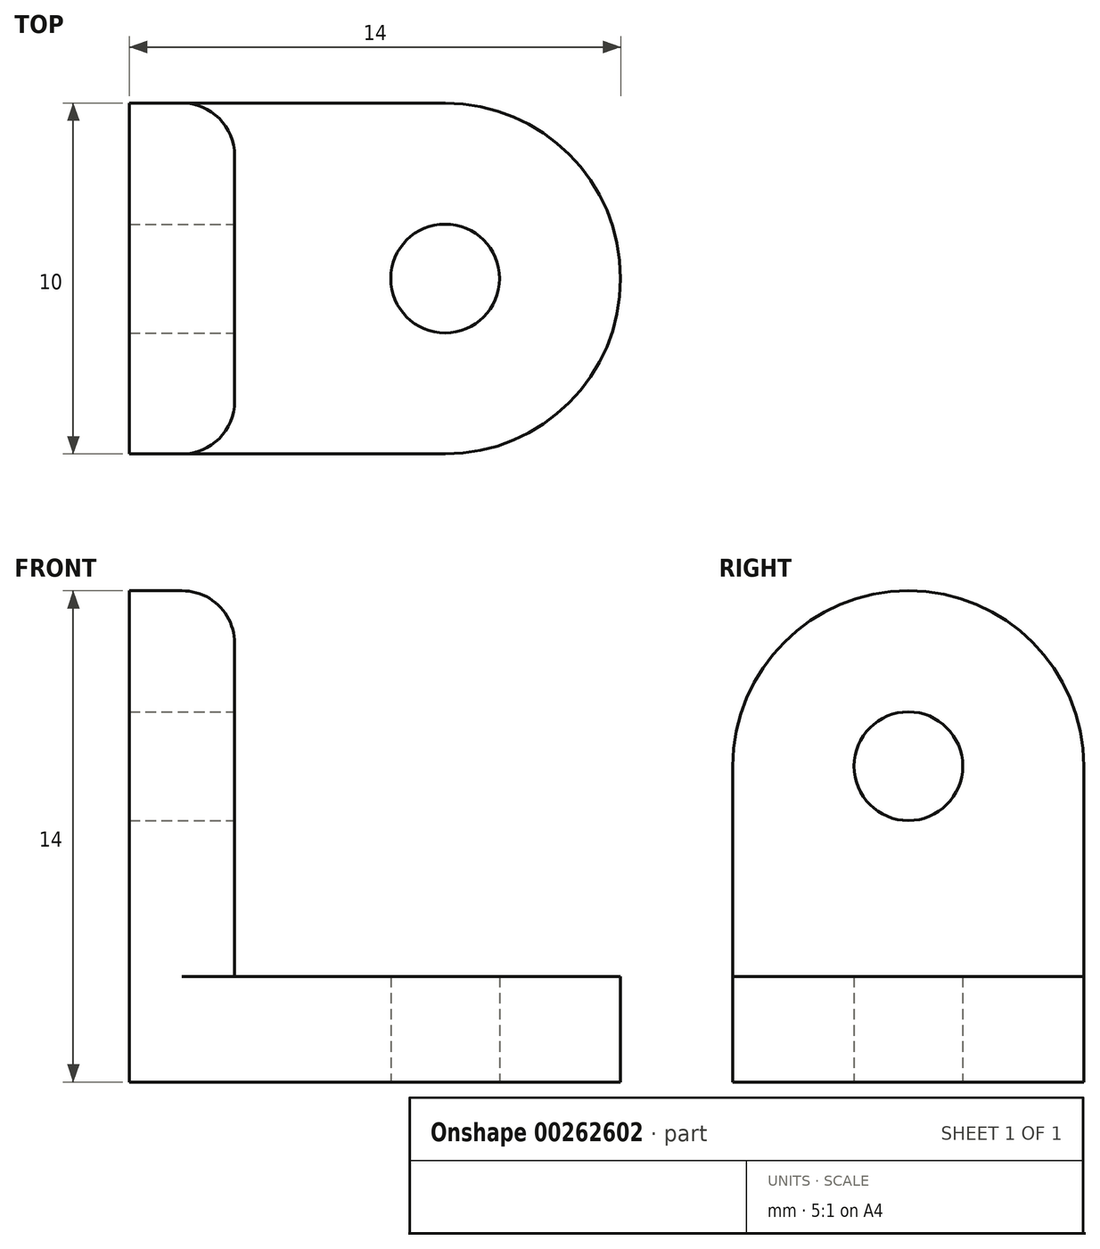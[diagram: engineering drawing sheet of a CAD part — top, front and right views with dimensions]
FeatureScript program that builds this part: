
annotation { "Feature Type Name" : "Feature", "Feature Type Description" : "" }
export const myFeature = defineFeature(function(context is Context, id is Id, definition is map)
    precondition{}
    {
        {
            var Q0;
            Q0=qCreatedBy(makeId("Top.planeOp"),FACE);
            var sketch = newSketch(context, id + "F0", { "sketchPlane" : qUnion([Q0])});
            skLineSegment(sketch, "E0.bottom", {"start": v(-7.9, -3.42) * mm, "end": v(1.1, -3.42) * mm});
            skLineSegment(sketch, "E0.top", {"start": v(-7.9, -8.42) * mm, "end": v(1.1, -8.42) * mm});
            skLineSegment(sketch, "E0.left", {"start": v(-7.9, -3.42) * mm, "end": v(-7.9, -8.42) * mm});
            skLineSegment(sketch, "E0.right", {"start": v(1.1, -3.42) * mm, "end": v(1.1, -8.42) * mm});
            skLineSegment(sketch, "E1", {"start": v(-7.9, -8.42) * mm, "end": v(-7.9, 1.58) * mm});
            skLineSegment(sketch, "E2", {"start": v(-7.9, 1.58) * mm, "end": v(1.1, 1.58) * mm});
            skLineSegment(sketch, "E3", {"start": v(6.1, -3.42) * mm, "end": v(6.1, -3.42) * mm});
            skLineSegment(sketch, "E4", {"start": v(1.1, -8.42) * mm, "end": v(-7.9, -8.42) * mm});
            skCircle(sketch, "E5", {"center": v(1.1, -3.42) * mm, "radius": 1.55 * mm});
            skLineSegment(sketch, "E6", {"start": v(-7.9, 1.58) * mm, "end": v(-4.9, 1.58) * mm});
            skLineSegment(sketch, "E7", {"start": v(-4.9, 1.58) * mm, "end": v(-4.9, -8.42) * mm});
            skPoint(sketch, "E8.visualSharp", {"position": v(6.1, 1.58) * mm});
            skArc(sketch, "E8.filletArc", {"start": v(6.1, -3.42) * mm, "mid": v(4.63, 0.11) * mm, "end": v(1.1, 1.58) * mm});
            skPoint(sketch, "E9.visualSharp", {"position": v(6.1, -8.42) * mm});
            skArc(sketch, "E9.filletArc", {"start": v(1.1, -8.42) * mm, "mid": v(4.63, -6.96) * mm, "end": v(6.1, -3.42) * mm});
            skSolve(sketch);
        }
        {
            var Q0;
            Q0 = qSketchRegion(id + "F0", true);
            extrude(context, id + "F1", {"entities" : qUnion([Q0]), "depth" : 3 * mm});
        }
        {
            var Q0;
            Q0=makeQuery(id+"F1.opExtrude","CAP_FACE",FACE,{"disambiguationData":[OSD([sQuery(id+"F0.wireOp",EDGE,"E1"),sQuery(id+"F0.wireOp",EDGE,"E2"),sQuery(id+"F0.wireOp",EDGE,"E4"),sQuery(id+"F0.wireOp",EDGE,"E5"),sQuery(id+"F0.wireOp",EDGE,"E6"),sQuery(id+"F0.wireOp",EDGE,"E8.filletArc"),sQuery(id+"F0.wireOp",EDGE,"E9.filletArc")])],"isStart":false});
            var sketch = newSketch(context, id + "F2", { "sketchPlane" : qUnion([Q0])});
            skLineSegment(sketch, "E10.bottom", {"start": v(-7.9, 1.58) * mm, "end": v(-4.9, 1.58) * mm});
            skLineSegment(sketch, "E10.top", {"start": v(-7.9, -8.42) * mm, "end": v(-4.9, -8.42) * mm});
            skLineSegment(sketch, "E10.left", {"start": v(-7.9, 1.58) * mm, "end": v(-7.9, -8.42) * mm});
            skLineSegment(sketch, "E10.right", {"start": v(-4.9, 1.58) * mm, "end": v(-4.9, -8.42) * mm});
            skSolve(sketch);
        }
        {
            var Q0;
            Q0=makeQuery(id+"F2.imprint","IMPRINT",FACE,{"disambiguationData":[TD([[makeQuery(id+"F2.imprint","IMPRINT",EDGE,{"derivedFrom":sQuery(id+"F2.wireOp",EDGE,"E10.bottom")}),-1.0]])]});
            extrude(context, id + "F3", {"entities" : qUnion([Q0]), "operationType" : NewBodyOperationType.ADD, "depth" : 11 * mm});
        }
        {
            var Q0;
            Q0=makeQuery(id+"F3.opExtrude","SWEPT_FACE",FACE,{"disambiguationData":[OSD([sQuery(id+"F2.wireOp",EDGE,"E10.right")])]});
            var sketch = newSketch(context, id + "F4", { "sketchPlane" : qUnion([Q0])});
            skLineSegment(sketch, "E11.bottom", {"start": v(1.58, 3) * mm, "end": v(-3.42, 3) * mm});
            skLineSegment(sketch, "E11.top", {"start": v(1.58, 9) * mm, "end": v(-3.42, 9) * mm});
            skLineSegment(sketch, "E11.left", {"start": v(1.58, 3) * mm, "end": v(1.58, 9) * mm});
            skLineSegment(sketch, "E11.right", {"start": v(-3.42, 3) * mm, "end": v(-3.42, 9) * mm});
            skCircle(sketch, "E12", {"center": v(-3.42, 9) * mm, "radius": 1.55 * mm});
            skSolve(sketch);
        }
        {
            var Q0;
            {var subQ0=sQuery(id+"F4.wireOp",EDGE,"E11.right");var subQ1=sQuery(id+"F4.wireOp",EDGE,"E11.top");var subQ2=makeQuery(id+"F4.imprint","INTERSECT",VERTEX,{"derivedFrom":[subQ1,subQ0]});Q0=makeQuery(id+"F4.imprint","IMPRINT",FACE,{"disambiguationData":[TD([[makeQuery(id+"F4.imprint","IMPRINT",EDGE,{"disambiguationData":[TD([[subQ2,1.0]])],"derivedFrom":subQ1}),-1.0]])]});}
            var Q1;
            {var subQ0=sQuery(id+"F4.wireOp",EDGE,"E11.right");var subQ1=sQuery(id+"F4.wireOp",EDGE,"E11.top");var subQ2=makeQuery(id+"F4.imprint","INTERSECT",VERTEX,{"derivedFrom":[subQ1,subQ0]});Q1=makeQuery(id+"F4.imprint","IMPRINT",FACE,{"disambiguationData":[TD([[makeQuery(id+"F4.imprint","IMPRINT",EDGE,{"disambiguationData":[TD([[subQ2,1.0]])],"derivedFrom":subQ1}),1.0]])]});}
            extrude(context, id + "F5", {"entities" : qUnion([Q0, Q1]), "operationType" : NewBodyOperationType.REMOVE, "oppositeDirection" : true, "depth" : 25 * mm});
        }
        {
            var Q0;
            Q0=makeQuery(id+"F3.opExtrude","CAP_EDGE",EDGE,{"disambiguationData":[OSD([sQuery(id+"F2.wireOp",EDGE,"E10.top")])],"isStart":false});
            var Q1;
            Q1=makeQuery(id+"F3.opExtrude","CAP_EDGE",EDGE,{"disambiguationData":[OSD([sQuery(id+"F2.wireOp",EDGE,"E10.bottom")])],"isStart":false});
            fillet(context, id + "F6", {"entities" : qUnion([Q0, Q1]), "radius" : 5 * mm, "tangentPropagation" : true, "allowEdgeOverflow" : false});
        }
        {
            var Q0;
            Q0=makeQuery(id+"F6.opFillet","BLEND_EDGE",EDGE,{"blendedFrom":[makeQuery(id+"F3.opExtrude","CAP_EDGE",EDGE,{"disambiguationData":[OSD([sQuery(id+"F2.wireOp",EDGE,"E10.top")])],"isStart":false}),makeQuery(id+"F3.opExtrude","SWEPT_FACE",FACE,{"disambiguationData":[OSD([sQuery(id+"F2.wireOp",EDGE,"E10.right")])]})],"blendedInto":[makeQuery(id+"F3.opExtrude","SWEPT_FACE",FACE,{"disambiguationData":[OSD([sQuery(id+"F2.wireOp",EDGE,"E10.right")])]})]});
            var Q1;
            Q1=makeQuery(id+"F3.opExtrude","SWEPT_EDGE",EDGE,{"disambiguationData":[OSD([sQuery(id+"F0.wireOp",EDGE,"E4"),sQuery(id+"F2.wireOp",EDGE,"E10.top"),sQuery(id+"F2.wireOp",EDGE,"E10.right")])]});
            var Q2;
            Q2=makeQuery(id+"F1.opExtrude","CAP_EDGE",EDGE,{"disambiguationData":[OSD([sQuery(id+"F0.wireOp",EDGE,"E4")])],"isStart":false});
            fillet(context, id + "F7", {"entities" : qUnion([Q0, Q1, Q2]), "radius" : 1.5 * mm, "tangentPropagation" : true, "allowEdgeOverflow" : false});
        }
    });
